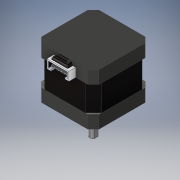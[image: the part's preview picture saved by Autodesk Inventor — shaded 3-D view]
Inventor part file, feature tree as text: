
AUTODESK INVENTOR PART (.ipt)
format: ipt  version: 2019 (Build 230136000, 136)  size: 358,400 bytes
history: native  units: mm
features: extrude x14, sketch x14, other x7, projected_geometry x5, thread x4, chamfer x2, pattern_circular x1, fillet x1, pattern_linear x1
ambient origin geometry x8: Origin, YZ Plane, XZ Plane, XY Plane, X Axis, Y Axis, Z Axis, Center Point
bodies: Body1 (feature_tree), Body2 (feature_tree), Body3 (feature_tree), Body4 (feature_tree), Body5 (feature_tree), Body6 (feature_tree), Body7 (feature_tree)
feature tree (49):
  other  "Bryła1"
  extrude  "Wyciągnięcie proste1"  Depth=42.3mm
  chamfer  "Faza1"  Distance=42.3mm
  extrude  "Wyciągnięcie proste2"  Depth=9.4mm TaperAngle=0.0deg
  extrude  "Wyciągnięcie proste3"  Depth=4.0mm TaperAngle=45.0deg
  extrude  "Wyciągnięcie proste4"  Depth=19.2mm TaperAngle=0.0deg
  extrude  "Wyciągnięcie proste5"  Depth=9.4mm TaperAngle=0.0deg
  extrude  "Wyciągnięcie proste6"  Depth=22.8mm
  extrude  "Wyciągnięcie proste7"  Depth=2.0mm TaperAngle=0.0deg
  extrude  "Wyciągnięcie proste8"  Depth=8.0mm
  extrude  "Wyciągnięcie proste9"  Depth=2.0mm TaperAngle=0.0deg
  pattern_circular  "Szyk kołowy1"  [2 undecoded]
  thread  "Gwint1"
  thread  "Gwint2"
  thread  "Gwint3"
  thread  "Gwint4"
  chamfer  "Faza2"  Distance=2.0mm
  extrude  "Wyciągnięcie proste10"  Depth=5.0mm
  extrude  "Wyciągnięcie proste11"  Depth=25.5mm TaperAngle=0.0deg
  fillet  "Zaokrąglenie1"  Radius=4.5mm
  extrude  "Wyciągnięcie proste12"  Depth=18.0mm TaperAngle=0.0deg
  extrude  "Wyciągnięcie proste13"  Depth=3.0mm
  extrude  "Wyciągnięcie proste14"  Depth=15.5mm
  pattern_linear  "Szyk prostokątny1"  Spacing1=15.5mm  [1 undecoded]
  sketch  "Szkic1"
  sketch  "Szkic2"
  projected_geometry  "Pętla rzutowana1"
  other  "Bryła2"
  sketch  "Szkic3"
  projected_geometry  "Pętla rzutowana2"
  other  "Bryła3"
  sketch  "Szkic4"
  sketch  "Szkic5"
  sketch  "Szkic6"
  sketch  "Szkic7"
  other  "Bryła4"
  sketch  "Szkic8"
  projected_geometry  "Pętla rzutowana3"
  sketch  "Szkic9"
  sketch  "Szkic10"
  other  "Bryła5"
  sketch  "Szkic11"
  other  "Bryła6"
  sketch  "Szkic12"
  projected_geometry  "Pętla rzutowana4"
  sketch  "Szkic13"
  sketch  "Szkic14"
  projected_geometry  "Pętla rzutowana5"
  other  "Bryła7"
note: 3 required parameter values undecoded (feature->parameter linkage not recoverable at this tier; creation-order binding heuristic only, values carry confidence <= 0.55)
